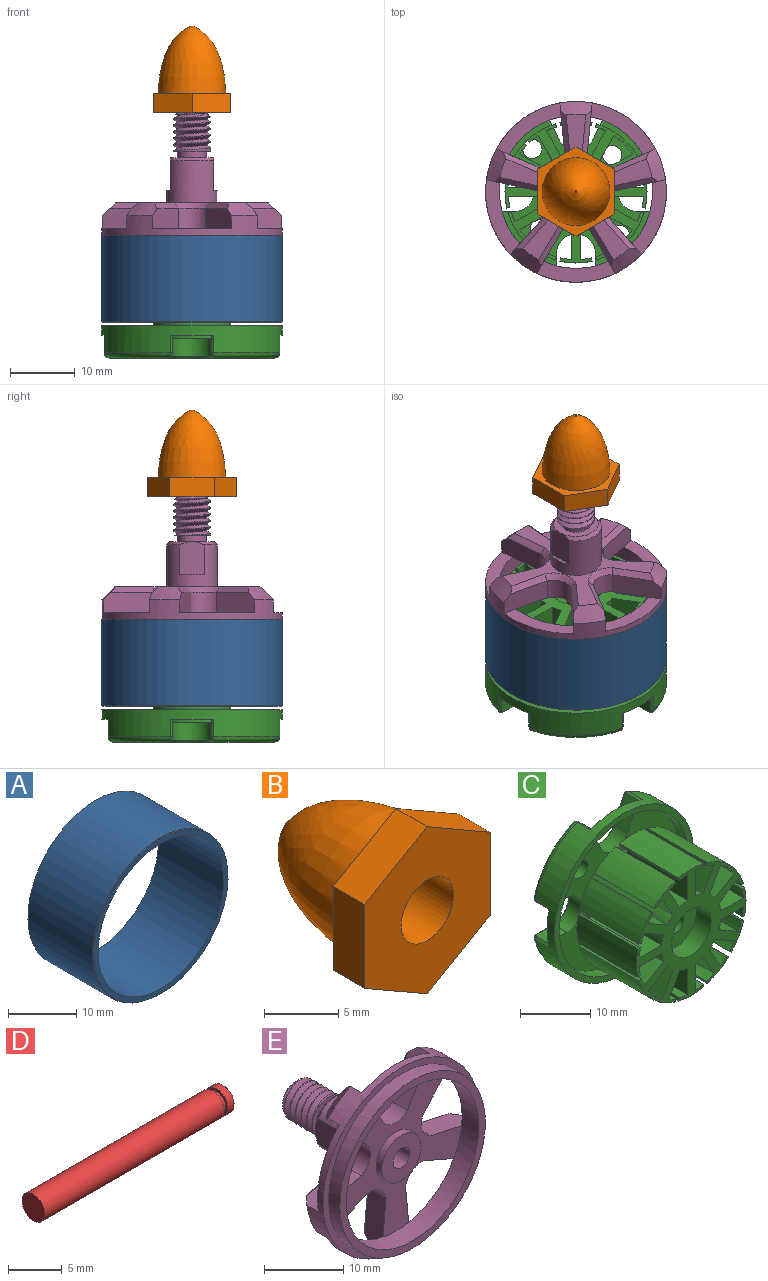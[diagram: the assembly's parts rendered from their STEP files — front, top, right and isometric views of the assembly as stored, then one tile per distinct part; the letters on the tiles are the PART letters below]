
ASSEMBLY  parts=5 mates=4
PART A: 5 faces, bbox 28x13.5x28 mm
  f0: plane 28x28mm, normal (0,1,0), area 84.8mm2, adj f2,f3
  f1: plane 27.8x27.8mm, normal (0,-1,0), area 76.1mm2, adj f3,f4
  f2: cylinder r=14mm len=28mm, axis (0,-1,0), area 1178.7mm2, adj f0,f4
  f3: cylinder r=13mm len=26mm, axis (0,-1,0), area 1102.7mm2, adj f0,f1
  f4: cone r=14mm half-angle=45deg, axis (0,1,0), area 12.4mm2, adj f1,f2
PART B: 13 faces, bbox 12x13.4x13.8 mm
  f0: plane 0.04x0.04mm, normal (0,1,0), area 0mm2, adj f1
  f1: torus R=0.02mm, axis (0,1,0), area 0mm2, adj f0
  f2: plane 5.98x3.45mm, normal (-0.5,0,0.87), area 20.7mm2, adj f3,f7,f9,f10
  f3: plane 6.9x3mm, normal (-1,0,0), area 20.7mm2, adj f2,f4,f7,f10
  f4: plane 5.98x3.45mm, normal (-0.5,0,-0.87), area 20.7mm2, adj f3,f5,f7,f10
  f5: plane 5.98x3.45mm, normal (0.5,0,-0.87), area 20.7mm2, adj f4,f6,f7,f10
  f6: plane 6.9x3mm, normal (1,0,0), area 20.7mm2, adj f5,f7,f9,f10
  f7: plane 13.8x11.95mm, normal (0,1,0), area 37.3mm2, adj f2,f3,f4,f5,f6,f8,f9
  f8: revolved ~10.49x10.49mm, area 0mm2, adj f7
  f9: plane 5.98x3.45mm, normal (0.5,0,0.87), area 20.7mm2, adj f2,f6,f7,f10
  f10: plane 13.8x11.95mm, normal (0,-1,0), area 104.1mm2, adj f2,f3,f4,f5,f6,f9,f11
  f11: cylinder r=2.5mm len=10mm, axis (0,-1,0), area 157.1mm2, adj f10,f12
  f12: plane 5x5mm, normal (0,-1,0), area 19.6mm2, adj f11
PART C: 164 faces, bbox 29.4x18.5x28.8 mm
  f0: cylinder r=1.5mm len=12.5mm, axis (0,1,0), area 117.8mm2, adj f26,f163
  f1: cylinder r=3mm len=5.43mm, axis (0,1,0), area 18.3mm2, adj f9,f17,f125,f133
  f2: cylinder r=3mm len=6mm, axis (0,1,0), area 25.4mm2, adj f11,f12,f125,f140
  f3: cylinder r=3mm len=6mm, axis (0,1,0), area 25.4mm2, adj f13,f14,f125,f154
  f4: cylinder r=3mm len=6mm, axis (0,1,0), area 25.4mm2, adj f15,f16,f125,f147
  f5: cylinder r=1.5mm len=3mm, axis (0,1,0), area 26.4mm2, adj f125,f160
  f6: cylinder r=1.5mm len=3mm, axis (0,1,0), area 26.4mm2, adj f125,f158
  f7: cylinder r=1.5mm len=3mm, axis (0,1,0), area 26.4mm2, adj f125,f161
  f8: cylinder r=1.5mm len=3mm, axis (0,1,0), area 26.4mm2, adj f125,f159
  f9: plane 4.6x3.2mm, normal (0.9,0,0.43), area 14mm2, adj f1,f19,f24,f125,f134,f135,f136
  f10: cylinder r=14mm len=28mm, axis (0,1,0), area 285.1mm2, adj f19,f20,f21,f22,f23,f126,f127,f128
  f11: plane 3.8x3.2mm, normal (0,0,-1), area 10.5mm2, adj f2,f20,f24,f125,f141,f142,f143
  f12: plane 3.8x3.2mm, normal (0,0,1), area 10.5mm2, adj f2,f20,f24,f125,f137,f138,f139
  f13: plane 3.8x3.2mm, normal (1,0,0), area 10.5mm2, adj f3,f21,f24,f125,f155,f156,f157
  f14: plane 3.8x3.2mm, normal (-1,0,0), area 10.5mm2, adj f3,f21,f24,f125,f151,f152,f153
  f15: plane 3.8x3.2mm, normal (0,0,1), area 10.5mm2, adj f4,f23,f24,f125,f144,f145,f146
  f16: plane 3.8x3.2mm, normal (0,0,-1), area 10.5mm2, adj f4,f23,f24,f125,f148,f149,f150
  f17: plane 4.6x3.2mm, normal (-0.9,0,0.43), area 14.1mm2, adj f1,f19,f24,f125,f130,f131,f132
  f18: plane 25.56x25.02mm, normal (0,1,0), area 291.6mm2, adj f25,f126,f127,f128,f129,f132,f133,f134
  f19: plane 10.53x1.83mm, normal (0,1,0), area 9.9mm2, adj f9,f10,f17,f24,f130,f136
  f20: plane 6.74x1.35mm, normal (0,1,0), area 6.2mm2, adj f10,f11,f12,f24,f137,f143
  f21: plane 6.74x1.35mm, normal (0,1,0), area 6.2mm2, adj f10,f13,f14,f24,f151,f157
  f22: plane 28x28mm, normal (0,-1,0), area 84.8mm2, adj f10,f24
  f23: plane 6.74x1.35mm, normal (0,1,0), area 6.2mm2, adj f10,f15,f16,f24,f144,f150
  f24: cylinder r=13mm len=26mm, axis (0,1,0), area 149.6mm2, adj f9,f11,f12,f13,f14,f15,f16,f17
  f25: cylinder r=4mm len=8mm, axis (0,1,0), area 75.4mm2, adj f18,f26
  f26: plane 8x8mm, normal (0,1,0), area 43.2mm2, adj f0,f25
  f27: plane 22x22mm, normal (0,-1,0), area 173.5mm2, adj f28,f29,f30,f31,f32,f33,f35,f36
  f28: cylinder r=6mm len=15.5mm, axis (0,1,0), area 367.8mm2, adj f27,f34,f35,f36,f42,f43,f44,f50
  f29: cylinder r=10.5mm len=12mm, axis (0,-1,0), area 19.9mm2, adj f27,f30,f34,f36
  f30: plane 12x0.49mm, normal (0.97,0,0.23), area 6mm2, adj f27,f29,f31,f34
  f31: cylinder r=11mm len=12mm, axis (0,-1,0), area 60.5mm2, adj f27,f30,f32,f34
  f32: plane 12x0.49mm, normal (-0.97,0,0.23), area 6mm2, adj f27,f31,f33,f34
  f33: cylinder r=10.5mm len=12mm, axis (0,-1,0), area 19.9mm2, adj f27,f32,f34,f35
  f34: plane 5.05x5mm, normal (0,1,0), area 9.2mm2, adj f28,f29,f30,f31,f32,f33,f35,f36
  f35: plane 12x4.52mm, normal (-1,0,0), area 54.2mm2, adj f27,f28,f33,f34
  f36: plane 12x4.52mm, normal (1,0,0), area 54.2mm2, adj f27,f28,f29,f34
  f37: cylinder r=10.5mm len=12mm, axis (0,-1,0), area 19.9mm2, adj f27,f38,f42,f43
  f38: plane 12x0.48mm, normal (0.96,0,-0.29), area 6mm2, adj f27,f37,f39,f42
  f39: cylinder r=11mm len=12mm, axis (0,-1,0), area 60.5mm2, adj f27,f38,f40,f42
  f40: plane 12x0.37mm, normal (-0.73,0,0.68), area 6mm2, adj f27,f39,f41,f42
  f41: cylinder r=10.5mm len=12mm, axis (0,-1,0), area 19.9mm2, adj f27,f40,f42,f44
  f42: plane 5.75x5.19mm, normal (0,1,0), area 9.2mm2, adj f28,f37,f38,f39,f40,f41,f43,f44
  f43: plane 12x3.91mm, normal (0.87,0,-0.5), area 54.2mm2, adj f27,f28,f37,f42
  f44: plane 12x3.91mm, normal (-0.87,0,0.5), area 54.2mm2, adj f27,f28,f41,f42
  f45: cylinder r=10.5mm len=12mm, axis (0,-1,0), area 19.9mm2, adj f27,f46,f50,f52
  f46: plane 12x0.37mm, normal (0.68,0,-0.73), area 6mm2, adj f27,f45,f47,f50
  f47: cylinder r=11mm len=12mm, axis (0,-1,0), area 60.5mm2, adj f27,f46,f48,f50
  f48: plane 12x0.48mm, normal (-0.29,0,0.96), area 6mm2, adj f27,f47,f49,f50
  f49: cylinder r=10.5mm len=12mm, axis (0,-1,0), area 19.9mm2, adj f27,f48,f50,f51
  f50: plane 5.75x5.19mm, normal (0,1,0), area 9.2mm2, adj f28,f45,f46,f47,f48,f49,f51,f52
  f51: plane 12x3.91mm, normal (-0.5,0,0.87), area 54.2mm2, adj f27,f28,f49,f50
  f52: plane 12x3.91mm, normal (0.5,0,-0.87), area 54.2mm2, adj f27,f28,f45,f50
  f53: cylinder r=10.5mm len=12mm, axis (0,-1,0), area 19.9mm2, adj f27,f54,f58,f60
  f54: plane 12x0.49mm, normal (0.23,0,-0.97), area 6mm2, adj f27,f53,f55,f58
  f55: cylinder r=11mm len=12mm, axis (0,-1,0), area 60.5mm2, adj f27,f54,f56,f58
  f56: plane 12x0.49mm, normal (0.23,0,0.97), area 6mm2, adj f27,f55,f57,f58
  f57: cylinder r=10.5mm len=12mm, axis (0,-1,0), area 19.9mm2, adj f27,f56,f58,f59
  f58: plane 5.05x5mm, normal (0,1,0), area 9.2mm2, adj f28,f53,f54,f55,f56,f57,f59,f60
  f59: plane 12x4.52mm, normal (0,0,1), area 54.2mm2, adj f27,f28,f57,f58
  f60: plane 12x4.52mm, normal (0,0,-1), area 54.2mm2, adj f27,f28,f53,f58
  f61: cylinder r=10.5mm len=12mm, axis (0,-1,0), area 19.9mm2, adj f27,f62,f66,f68
  f62: plane 12x0.48mm, normal (-0.29,0,-0.96), area 6mm2, adj f27,f61,f63,f66
  f63: cylinder r=11mm len=12mm, axis (0,-1,0), area 60.5mm2, adj f27,f62,f64,f66
  f64: plane 12x0.37mm, normal (0.68,0,0.73), area 6mm2, adj f27,f63,f65,f66
  f65: cylinder r=10.5mm len=12mm, axis (0,-1,0), area 19.9mm2, adj f27,f64,f66,f67
  f66: plane 5.75x5.19mm, normal (0,1,0), area 9.2mm2, adj f28,f61,f62,f63,f64,f65,f67,f68
  f67: plane 12x3.91mm, normal (0.5,0,0.87), area 54.2mm2, adj f27,f28,f65,f66
  f68: plane 12x3.91mm, normal (-0.5,0,-0.87), area 54.2mm2, adj f27,f28,f61,f66
  f69: cylinder r=10.5mm len=12mm, axis (0,-1,0), area 19.9mm2, adj f27,f70,f74,f76
  f70: plane 12x0.37mm, normal (-0.73,0,-0.68), area 6mm2, adj f27,f69,f71,f74
  f71: cylinder r=11mm len=12mm, axis (0,-1,0), area 60.5mm2, adj f27,f70,f72,f74
  f72: plane 12x0.48mm, normal (0.96,0,0.29), area 6mm2, adj f27,f71,f73,f74
  f73: cylinder r=10.5mm len=12mm, axis (0,-1,0), area 19.9mm2, adj f27,f72,f74,f75
  f74: plane 5.75x5.19mm, normal (0,1,0), area 9.2mm2, adj f28,f69,f70,f71,f72,f73,f75,f76
  f75: plane 12x3.91mm, normal (0.87,0,0.5), area 54.2mm2, adj f27,f28,f73,f74
  f76: plane 12x3.91mm, normal (-0.87,0,-0.5), area 54.2mm2, adj f27,f28,f69,f74
  f77: cylinder r=10.5mm len=12mm, axis (0,-1,0), area 19.9mm2, adj f27,f78,f82,f84
  f78: plane 12x0.49mm, normal (-0.97,0,-0.23), area 6mm2, adj f27,f77,f79,f82
  f79: cylinder r=11mm len=12mm, axis (0,-1,0), area 60.5mm2, adj f27,f78,f80,f82
  f80: plane 12x0.49mm, normal (0.97,0,-0.23), area 6mm2, adj f27,f79,f81,f82
  f81: cylinder r=10.5mm len=12mm, axis (0,-1,0), area 19.9mm2, adj f27,f80,f82,f83
  f82: plane 5.05x5mm, normal (0,1,0), area 9.2mm2, adj f28,f77,f78,f79,f80,f81,f83,f84
  f83: plane 12x4.52mm, normal (1,0,0), area 54.2mm2, adj f27,f28,f81,f82
  f84: plane 12x4.52mm, normal (-1,0,0), area 54.2mm2, adj f27,f28,f77,f82
  f85: cylinder r=10.5mm len=12mm, axis (0,-1,0), area 19.9mm2, adj f27,f86,f90,f92
  f86: plane 12x0.48mm, normal (-0.96,0,0.29), area 6mm2, adj f27,f85,f87,f90
  f87: cylinder r=11mm len=12mm, axis (0,-1,0), area 60.5mm2, adj f27,f86,f88,f90
  f88: plane 12x0.37mm, normal (0.73,0,-0.68), area 6mm2, adj f27,f87,f89,f90
  f89: cylinder r=10.5mm len=12mm, axis (0,-1,0), area 19.9mm2, adj f27,f88,f90,f91
  f90: plane 5.75x5.19mm, normal (0,1,0), area 9.2mm2, adj f28,f85,f86,f87,f88,f89,f91,f92
  f91: plane 12x3.91mm, normal (0.87,0,-0.5), area 54.2mm2, adj f27,f28,f89,f90
  f92: plane 12x3.91mm, normal (-0.87,0,0.5), area 54.2mm2, adj f27,f28,f85,f90
  f93: cylinder r=10.5mm len=12mm, axis (0,-1,0), area 19.9mm2, adj f27,f94,f98,f100
  f94: plane 12x0.37mm, normal (-0.68,0,0.73), area 6mm2, adj f27,f93,f95,f98
  f95: cylinder r=11mm len=12mm, axis (0,-1,0), area 60.5mm2, adj f27,f94,f96,f98
  f96: plane 12x0.48mm, normal (0.29,0,-0.96), area 6mm2, adj f27,f95,f97,f98
  f97: cylinder r=10.5mm len=12mm, axis (0,-1,0), area 19.9mm2, adj f27,f96,f98,f99
  f98: plane 5.75x5.19mm, normal (0,1,0), area 9.2mm2, adj f28,f93,f94,f95,f96,f97,f99,f100
  f99: plane 12x3.91mm, normal (0.5,0,-0.87), area 54.2mm2, adj f27,f28,f97,f98
  f100: plane 12x3.91mm, normal (-0.5,0,0.87), area 54.2mm2, adj f27,f28,f93,f98
  f101: cylinder r=10.5mm len=12mm, axis (0,-1,0), area 19.9mm2, adj f27,f102,f106,f108
  f102: plane 12x0.49mm, normal (-0.23,0,0.97), area 6mm2, adj f27,f101,f103,f106
  f103: cylinder r=11mm len=12mm, axis (0,-1,0), area 60.5mm2, adj f27,f102,f104,f106
  f104: plane 12x0.49mm, normal (-0.23,0,-0.97), area 6mm2, adj f27,f103,f105,f106
  f105: cylinder r=10.5mm len=12mm, axis (0,-1,0), area 19.9mm2, adj f27,f104,f106,f107
  f106: plane 5.05x5mm, normal (0,1,0), area 9.2mm2, adj f28,f101,f102,f103,f104,f105,f107,f108
  f107: plane 12x4.52mm, normal (0,0,-1), area 54.2mm2, adj f27,f28,f105,f106
  f108: plane 12x4.52mm, normal (0,0,1), area 54.2mm2, adj f27,f28,f101,f106
  f109: cylinder r=10.5mm len=12mm, axis (0,-1,0), area 19.9mm2, adj f27,f110,f114,f116
  f110: plane 12x0.48mm, normal (0.29,0,0.96), area 6mm2, adj f27,f109,f111,f114
  f111: cylinder r=11mm len=12mm, axis (0,-1,0), area 60.5mm2, adj f27,f110,f112,f114
  f112: plane 12x0.37mm, normal (-0.68,0,-0.73), area 6mm2, adj f27,f111,f113,f114
  f113: cylinder r=10.5mm len=12mm, axis (0,-1,0), area 19.9mm2, adj f27,f112,f114,f115
  f114: plane 5.75x5.19mm, normal (0,1,0), area 9.2mm2, adj f28,f109,f110,f111,f112,f113,f115,f116
  f115: plane 12x3.91mm, normal (-0.5,0,-0.87), area 54.2mm2, adj f27,f28,f113,f114
  f116: plane 12x3.91mm, normal (0.5,0,0.87), area 54.2mm2, adj f27,f28,f109,f114
  f117: plane 5.75x5.19mm, normal (0,1,0), area 9.2mm2, adj f28,f118,f119,f120,f121,f122,f123,f124
  f118: plane 12x3.91mm, normal (0.87,0,0.5), area 54.2mm2, adj f27,f28,f117,f119
  f119: cylinder r=10.5mm len=12mm, axis (0,-1,0), area 19.9mm2, adj f27,f117,f118,f120
  f120: plane 12x0.37mm, normal (0.73,0,0.68), area 6mm2, adj f27,f117,f119,f121
  f121: cylinder r=11mm len=12mm, axis (0,-1,0), area 60.5mm2, adj f27,f117,f120,f122
  f122: plane 12x0.48mm, normal (-0.96,0,-0.29), area 6mm2, adj f27,f117,f121,f123
  f123: cylinder r=10.5mm len=12mm, axis (0,-1,0), area 19.9mm2, adj f27,f117,f122,f124
  f124: plane 12x3.91mm, normal (-0.87,0,-0.5), area 54.2mm2, adj f27,f28,f117,f123
  f125: plane 25.3x24.82mm, normal (0,-1,0), area 245.7mm2, adj f1,f2,f3,f4,f5,f6,f7,f8
  f126: torus R=13.2mm, axis (0,1,0), area 18.5mm2, adj f10,f18,f138,f156
  f127: torus R=13.2mm, axis (0,1,0), area 16.2mm2, adj f10,f18,f135,f142
  f128: torus R=13.2mm, axis (0,1,0), area 16.2mm2, adj f10,f18,f131,f149
  f129: torus R=13.2mm, axis (0,1,0), area 18.5mm2, adj f10,f18,f145,f152
  f130: plane 2.7x0.38mm, normal (-0.36,0,0.93), area 1.1mm2, adj f10,f17,f19,f131
  f131: bspline ~0.8x0.73mm, area 0.4mm2, adj f17,f128,f130,f132
  f132: plane 4.28x2.22mm, normal (-0.64,0.71,0.3), area 1.9mm2, adj f17,f18,f131,f133
  f133: cone r=3.3mm half-angle=45deg, axis (0,1,0), area 3mm2, adj f1,f18,f132,f134
  f134: plane 4.28x2.22mm, normal (0.64,0.71,0.3), area 1.9mm2, adj f9,f18,f133,f135
  f135: bspline ~0.8x0.73mm, area 0.4mm2, adj f9,f127,f134,f136
  f136: plane 2.7x0.38mm, normal (0.36,0,0.93), area 1.1mm2, adj f9,f10,f19,f135
  f137: plane 2.7x0.37mm, normal (-0.79,0,0.62), area 1.3mm2, adj f10,f12,f20,f138
  f138: bspline ~0.81x0.8mm, area 0.5mm2, adj f12,f126,f137,f139
  f139: plane 3.28x0.3mm, normal (0,0.71,0.71), area 1.4mm2, adj f12,f18,f138,f140
  f140: cone r=3.3mm half-angle=45deg, axis (0,1,0), area 4.2mm2, adj f2,f18,f139,f141
  f141: plane 3.28x0.3mm, normal (0,0.71,-0.71), area 1.4mm2, adj f11,f18,f140,f142
  f142: bspline ~0.81x0.8mm, area 0.5mm2, adj f11,f127,f141,f143
  f143: plane 2.7x0.37mm, normal (-0.79,0,-0.62), area 1.3mm2, adj f10,f11,f20,f142
  f144: plane 2.7x0.37mm, normal (0.79,0,0.62), area 1.3mm2, adj f10,f15,f23,f145
  f145: bspline ~0.81x0.8mm, area 0.5mm2, adj f15,f129,f144,f146
  f146: plane 3.28x0.3mm, normal (0,0.71,0.71), area 1.4mm2, adj f15,f18,f145,f147
  f147: cone r=3.3mm half-angle=45deg, axis (0,1,0), area 4.2mm2, adj f4,f18,f146,f148
  f148: plane 3.28x0.3mm, normal (0,0.71,-0.71), area 1.4mm2, adj f16,f18,f147,f149
  f149: bspline ~0.81x0.8mm, area 0.5mm2, adj f16,f128,f148,f150
  f150: plane 2.7x0.37mm, normal (0.79,0,-0.62), area 1.3mm2, adj f10,f16,f23,f149
  f151: plane 2.7x0.37mm, normal (-0.62,0,-0.79), area 1.3mm2, adj f10,f14,f21,f152
  f152: bspline ~0.81x0.8mm, area 0.5mm2, adj f14,f129,f151,f153
  f153: plane 3.28x0.3mm, normal (-0.71,0.71,0), area 1.4mm2, adj f14,f18,f152,f154
  f154: cone r=3.3mm half-angle=45deg, axis (0,1,0), area 4.2mm2, adj f3,f18,f153,f155
  f155: plane 3.28x0.3mm, normal (0.71,0.71,0), area 1.4mm2, adj f13,f18,f154,f156
  f156: bspline ~0.81x0.8mm, area 0.5mm2, adj f13,f126,f155,f157
  f157: plane 2.7x0.37mm, normal (0.62,0,-0.79), area 1.3mm2, adj f10,f13,f21,f156
  f158: cone r=1.5mm half-angle=45deg, axis (0,1,0), area 2.8mm2, adj f6,f18
  f159: cone r=1.5mm half-angle=45deg, axis (0,1,0), area 2.8mm2, adj f8,f18
  f160: cone r=1.5mm half-angle=45deg, axis (0,1,0), area 2.8mm2, adj f5,f18
  f161: cone r=1.5mm half-angle=45deg, axis (0,1,0), area 2.8mm2, adj f7,f18
  f162: cylinder r=4mm len=8mm, axis (0,-1,0), area 75.4mm2, adj f27,f163
  f163: plane 8x8mm, normal (0,-1,0), area 43.2mm2, adj f0,f162
PART D: 8 faces, bbox 25x3x3 mm
  f0: plane 3x3mm, normal (-1,0,0), area 7.1mm2, adj f6
  f1: plane 2.6x2.6mm, normal (1,0,0), area 5.3mm2, adj f7
  f2: cylinder r=1.5mm len=3mm, axis (-1,0,0), area 7.5mm2, adj f3,f7
  f3: plane 3x3mm, normal (-1,0,0), area 2.6mm2, adj f2,f4
  f4: cylinder r=1.2mm len=2.4mm, axis (-1,0,0), area 3.8mm2, adj f3,f5
  f5: plane 3x3mm, normal (1,0,0), area 2.6mm2, adj f4,f6
  f6: cylinder r=1.5mm len=23.5mm, axis (-1,0,0), area 221.5mm2, adj f0,f5
  f7: cone r=1.5mm half-angle=45deg, axis (-1,0,0), area 2.5mm2, adj f1,f2
PART E: 68 faces, bbox 28.5x21.9x28.5 mm
  f0: cone r=3.43mm half-angle=45deg, axis (0,-1,0), area 6.5mm2, adj f46,f47,f65,f67
  f1: plane 28x28mm, normal (0,-1,0), area 84.8mm2, adj f6,f54
  f2: plane 10.03x8mm, normal (0,1,0), area 24.5mm2, adj f6,f8,f21,f23
  f3: plane 11.55x5.31mm, normal (0,1,0), area 24.5mm2, adj f6,f8,f18,f20
  f4: plane 12.15x3.25mm, normal (0,1,0), area 24.5mm2, adj f6,f8,f15,f17
  f5: plane 11.55x5.31mm, normal (0,1,0), area 24.5mm2, adj f6,f8,f12,f14
  f6: cylinder r=14mm len=28mm, axis (0,1,0), area 138.3mm2, adj f1,f2,f3,f4,f5,f7,f9,f11
  f7: plane 10.03x8mm, normal (0,1,0), area 24.5mm2, adj f6,f8,f9,f11
  f8: cylinder r=11.85mm len=23.7mm, axis (0,1,0), area 223.4mm2, adj f2,f3,f4,f5,f7,f25,f53
  f9: plane 7.85x3.2mm, normal (-1,0,0.1), area 24.5mm2, adj f6,f7,f10,f25,f40,f44
  f10: cylinder r=2.83mm len=3.34mm, axis (0,-1,0), area 14.8mm2, adj f9,f11,f25,f39
  f11: plane 7.24x3.2mm, normal (0.4,0,-0.92), area 24.5mm2, adj f6,f7,f10,f25,f38,f45
  f12: plane 7.7x3.2mm, normal (-0.22,0,0.98), area 24.5mm2, adj f5,f6,f13,f25,f35,f45
  f13: cylinder r=2.83mm len=3.93mm, axis (0,-1,0), area 14.8mm2, adj f12,f14,f25,f36
  f14: plane 5.91x5.23mm, normal (-0.75,0,-0.66), area 24.5mm2, adj f5,f6,f13,f25,f37,f41
  f15: plane 6.8x4.01mm, normal (0.86,0,0.51), area 24.5mm2, adj f4,f6,f16,f25,f28,f41
  f16: cylinder r=2.83mm len=4.13mm, axis (0,-1,0), area 14.8mm2, adj f15,f17,f25,f27
  f17: plane 6.8x4.01mm, normal (-0.86,0,0.51), area 24.5mm2, adj f4,f6,f16,f25,f26,f42
  f18: plane 5.91x5.23mm, normal (0.75,0,-0.66), area 24.5mm2, adj f3,f6,f19,f25,f31,f42
  f19: cylinder r=2.83mm len=3.93mm, axis (0,-1,0), area 14.8mm2, adj f18,f20,f25,f30
  f20: plane 7.7x3.2mm, normal (0.22,0,0.98), area 24.5mm2, adj f3,f6,f19,f25,f29,f43
  f21: plane 7.24x3.2mm, normal (-0.4,0,-0.92), area 24.5mm2, adj f2,f6,f22,f25,f34,f43
  f22: cylinder r=2.83mm len=3.34mm, axis (0,-1,0), area 14.8mm2, adj f21,f23,f25,f33
  f23: plane 7.85x3.2mm, normal (1,0,0.1), area 24.5mm2, adj f2,f6,f22,f25,f32,f44
  f24: plane 23.58x22.52mm, normal (0,1,0), area 103.9mm2, adj f26,f27,f28,f29,f30,f31,f32,f33
  f25: plane 23.53x22.6mm, normal (0,-1,0), area 179.5mm2, adj f8,f9,f10,f11,f12,f13,f14,f15
  f26: plane 6.25x3.72mm, normal (-0.61,0.71,0.36), area 7.2mm2, adj f17,f24,f27,f42
  f27: cone r=3.63mm half-angle=45deg, axis (0,1,0), area 6.1mm2, adj f16,f24,f26,f28
  f28: plane 6.25x3.72mm, normal (0.61,0.71,0.36), area 7.2mm2, adj f15,f24,f27,f41
  f29: plane 6.8x2.09mm, normal (0.15,0.71,0.69), area 7.2mm2, adj f20,f24,f30,f43
  f30: cone r=3.63mm half-angle=45deg, axis (0,1,0), area 6.1mm2, adj f19,f24,f29,f31
  f31: plane 5.1x5.03mm, normal (0.53,0.71,-0.47), area 7.2mm2, adj f18,f24,f30,f42
  f32: plane 6.68x1.46mm, normal (0.7,0.71,0.07), area 7.2mm2, adj f23,f24,f33,f44
  f33: cone r=3.63mm half-angle=45deg, axis (0,1,0), area 6.1mm2, adj f22,f24,f32,f34
  f34: plane 6.15x3.45mm, normal (-0.28,0.71,-0.65), area 7.2mm2, adj f21,f24,f33,f43
  f35: plane 6.8x2.09mm, normal (-0.15,0.71,0.69), area 7.2mm2, adj f12,f24,f36,f45
  f36: cone r=3.63mm half-angle=45deg, axis (0,1,0), area 6.1mm2, adj f13,f24,f35,f37
  f37: plane 5.1x5.03mm, normal (-0.53,0.71,-0.47), area 7.2mm2, adj f14,f24,f36,f41
  f38: plane 6.15x3.45mm, normal (0.28,0.71,-0.65), area 7.2mm2, adj f11,f24,f39,f45
  f39: cone r=3.63mm half-angle=45deg, axis (0,1,0), area 6.1mm2, adj f10,f24,f38,f40
  f40: plane 6.68x1.46mm, normal (-0.7,0.71,0.07), area 7.2mm2, adj f9,f24,f39,f44
  f41: cone r=12mm half-angle=45deg, axis (0,-1,0), area 12.8mm2, adj f6,f14,f15,f24,f28,f37
  f42: cone r=12mm half-angle=45deg, axis (0,-1,0), area 12.8mm2, adj f6,f17,f18,f24,f26,f31
  f43: cone r=12mm half-angle=45deg, axis (0,-1,0), area 12.8mm2, adj f6,f20,f21,f24,f29,f34
  f44: cone r=12mm half-angle=45deg, axis (0,-1,0), area 12.8mm2, adj f6,f9,f23,f24,f32,f40
  f45: cone r=12mm half-angle=45deg, axis (0,-1,0), area 12.8mm2, adj f6,f11,f12,f24,f35,f38
  f46: cylinder r=3.92mm len=7.85mm, axis (0,-1,0), area 123.3mm2, adj f0,f24,f48,f64,f65,f66,f67
  f47: plane 6.85x6.8mm, normal (0,1,0), area 20.9mm2, adj f0,f48,f56,f65,f67
  f48: cone r=3.43mm half-angle=45deg, axis (0,-1,0), area 6.5mm2, adj f46,f47,f65,f67
  f49: cylinder r=3.5mm len=7mm, axis (0,1,0), area 22mm2, adj f25,f50
  f50: plane 7x7mm, normal (0,-1,0), area 31.4mm2, adj f49,f51
  f51: cylinder r=1.5mm len=10mm, axis (0,-1,0), area 94.2mm2, adj f50,f52
  f52: plane 3x3mm, normal (0,-1,0), area 7.1mm2, adj f51
  f53: plane 26x26mm, normal (0,-1,0), area 89.8mm2, adj f8,f54
  f54: cylinder r=13mm len=26mm, axis (0,1,0), area 163.4mm2, adj f1,f53
  f55: plane 6.3x6.02mm, normal (0,-1,0), area 8.5mm2, adj f56,f60,f61,f62,f63
  f56: cylinder r=2.25mm len=4.5mm, axis (0,1,0), area 14.1mm2, adj f47,f55
  f57: plane 4.45x4.45mm, normal (0,1,0), area 15.6mm2, adj f59
  f58: cone r=2.23mm half-angle=45deg, axis (0,-1,0), area 1.5mm2, adj f59,f60,f61,f63
  f59: cone r=2.23mm half-angle=45deg, axis (0,-1,0), area 7.5mm2, adj f57,f58,f61
  f60: bspline ~6.49x5.98mm, area 72.4mm2, adj f55,f58,f61,f63
  f61: bspline ~6.49x5.98mm, area 69.6mm2, adj f55,f58,f59,f60,f62,f63
  f62: plane 0.65x0.44mm, normal (0,0,-1), area 0.1mm2, adj f55,f61,f63
  f63: cylinder r=2.93mm len=5.85mm, axis (0,-1,0), area 12.1mm2, adj f55,f58,f60,f61,f62
  f64: plane 3.92x0.53mm, normal (0,1,0), area 1.4mm2, adj f46,f65
  f65: plane 5.24x4.16mm, normal (1,0,0), area 19mm2, adj f0,f46,f47,f48,f64
  f66: plane 3.92x0.53mm, normal (0,1,0), area 1.4mm2, adj f46,f67
  f67: plane 5.24x4.16mm, normal (-1,0,0), area 19mm2, adj f0,f46,f47,f48,f66
PLACE A rot(axis=(1,0,0),90deg) t=(0,1.8,-34.01)mm
PLACE B rot(axis=(1,0,0),90deg) t=(0,1.8,-1.51)mm
PLACE C rot(axis=(-1,0,0),90deg) t=(0,1.8,-39.51)mm
PLACE D rot(axis=(-0.71,0,0.71),180deg) t=(0,1.8,-14.51)mm
PLACE E rot(axis=(1,0,0),90deg) t=(0,1.8,-19.51)mm
MATE fastened A.f2 <-> E.f0  axis (0,0,1) through (0,1.8,-20.51)mm
MATE fastened D.f2 <-> E.f0  axis (0,0,1) through (0,1.8,-14.51)mm
MATE fastened E.f0 <-> B.f11  axis (0,0,1) through (0,1.8,-1.51)mm
MATE revolute D.f2 <-> C.f0  axis (0,0,-1) through (0,1.8,-39.51)mm
